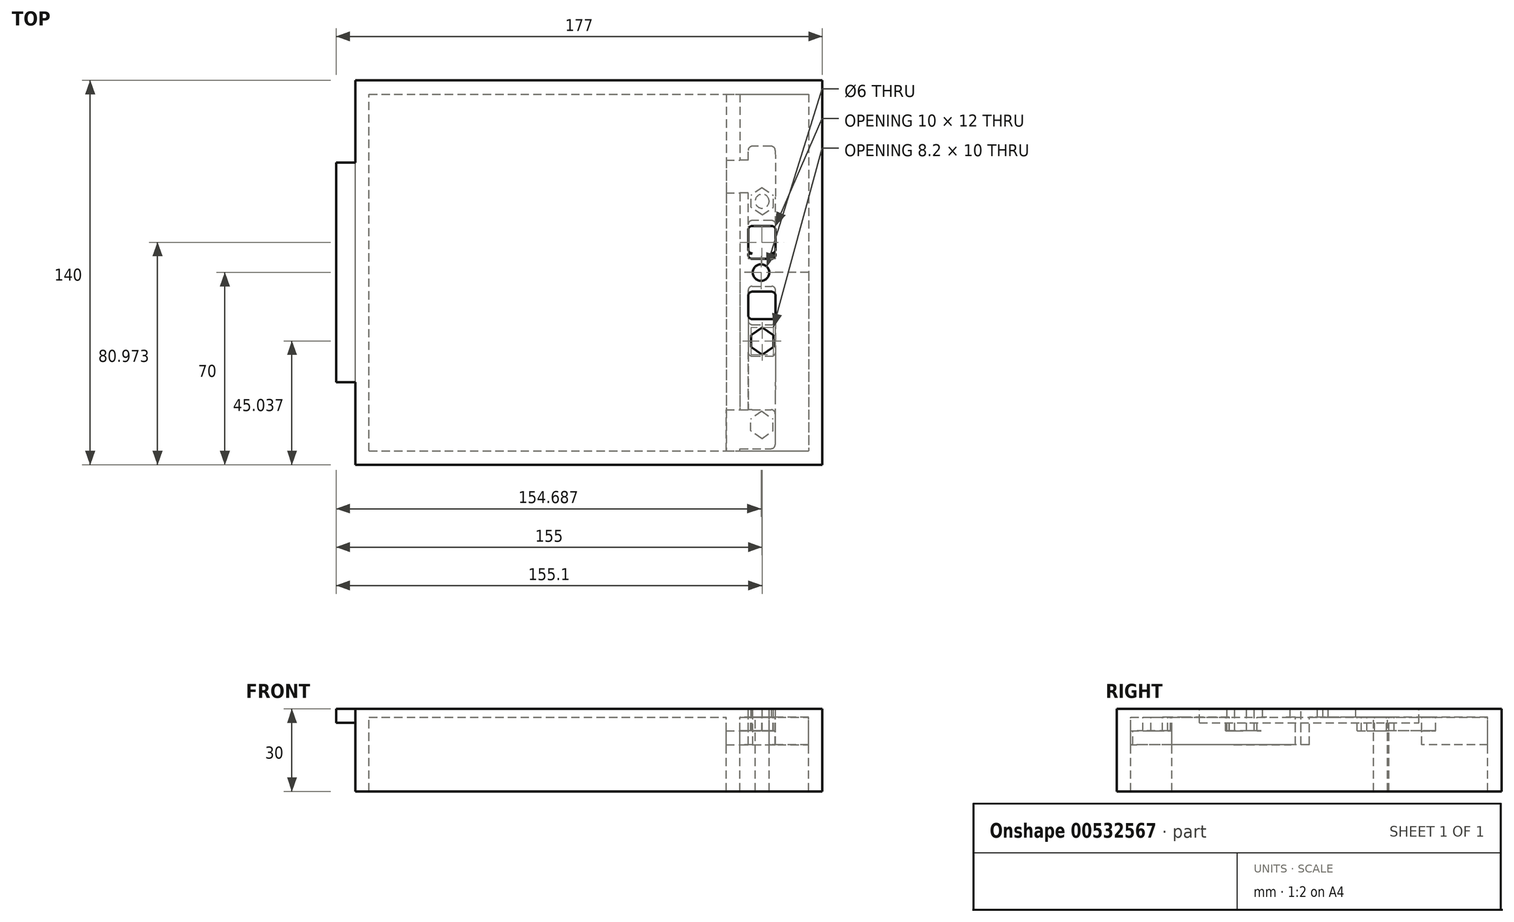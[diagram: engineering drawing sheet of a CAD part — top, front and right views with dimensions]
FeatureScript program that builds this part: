
annotation { "Feature Type Name" : "Feature", "Feature Type Description" : "" }
export const myFeature = defineFeature(function(context is Context, id is Id, definition is map)
    precondition{}
    {
        {
            var Q0;
            Q0=qCreatedBy(makeId("Top.planeOp"),FACE);
            var sketch = newSketch(context, id + "F0", { "sketchPlane" : qUnion([Q0])});
            skLineSegment(sketch, "E0.bottom", {"start": v(-87.5, 70) * mm, "end": v(82.5, 70) * mm});
            skLineSegment(sketch, "E0.top", {"start": v(-82.5, 0) * mm, "end": v(82.5, 0) * mm, "construction": true});
            skLineSegment(sketch, "E0.right", {"start": v(82.5, 70) * mm, "end": v(82.5, 0) * mm});
            skLineSegment(sketch, "E1.bottom", {"start": v(-82.5, 65) * mm, "end": v(77.5, 65) * mm});
            skLineSegment(sketch, "E1.left", {"start": v(-87.5, 65) * mm, "end": v(-87.5, -5) * mm});
            skLineSegment(sketch, "E1.right", {"start": v(77.5, 65) * mm, "end": v(77.5, 0) * mm});
            skLineSegment(sketch, "E2.left", {"start": v(47.5, 65) * mm, "end": v(47.5, 0.9) * mm});
            skLineSegment(sketch, "E2.right", {"start": v(52.5, 65) * mm, "end": v(52.5, 0) * mm});
            skLineSegment(sketch, "E3", {"start": v(47.5, 41) * mm, "end": v(52.5, 41) * mm});
            skLineSegment(sketch, "E4.MirrorCS", {"start": v(47.5, -65) * mm, "end": v(52.5, -65) * mm});
            skLineSegment(sketch, "E5.MirrorCS", {"start": v(47.5, -65) * mm, "end": v(47.5, -0.9) * mm});
            skLineSegment(sketch, "E6.MirrorCS", {"start": v(-82.5, -65) * mm, "end": v(77.5, -65) * mm});
            skLineSegment(sketch, "E7.MirrorCS", {"start": v(-87.5, -65) * mm, "end": v(-87.5, 5) * mm});
            skLineSegment(sketch, "E8.MirrorCS", {"start": v(-87.5, -70) * mm, "end": v(82.5, -70) * mm});
            skLineSegment(sketch, "E9.MirrorCS", {"start": v(82.5, -70) * mm, "end": v(82.5, 0) * mm});
            skLineSegment(sketch, "E10.MirrorCS", {"start": v(57, -4.97) * mm, "end": v(64, -4.97) * mm});
            skLineSegment(sketch, "E11.MirrorCS", {"start": v(55.5, -15.47) * mm, "end": v(55.5, -8.47) * mm});
            skLineSegment(sketch, "E12.MirrorCS", {"start": v(77.5, -65) * mm, "end": v(77.5, 0) * mm});
            skLineSegment(sketch, "E13.MirrorCS", {"start": v(65.5, -15.47) * mm, "end": v(65.5, -8.47) * mm});
            skLineSegment(sketch, "E14.MirrorCS", {"start": v(52.5, -65) * mm, "end": v(52.5, 0) * mm});
            skLineSegment(sketch, "E15", {"start": v(-87.5, -65) * mm, "end": v(-87.5, -70) * mm});
            skLineSegment(sketch, "E16", {"start": v(-87.5, 65) * mm, "end": v(-87.5, 70) * mm});
            skLineSegment(sketch, "E17.left", {"start": v(-177.5, 47.5) * mm, "end": v(-177.5, 0) * mm});
            skCircle(sketch, "E18", {"center": v(-162.5, 30) * mm, "radius": 3.25 * mm});
            skLineSegment(sketch, "E19.left", {"start": v(-147.5, 70) * mm, "end": v(-147.5, 0) * mm});
            skCircle(sketch, "E20.MirrorC", {"center": v(-162.5, -30) * mm, "radius": 3.25 * mm});
            skLineSegment(sketch, "E21.MirrorCS", {"start": v(-147.5, -70) * mm, "end": v(-147.5, 0) * mm});
            skLineSegment(sketch, "E22.MirrorCS", {"start": v(-177.5, -47.5) * mm, "end": v(-177.5, 0) * mm});
            skCircle(sketch, "E23", {"center": v(-162.5, 30) * mm, "radius": 12.5 * mm});
            skCircle(sketch, "E24.MirrorC", {"center": v(-162.5, -30) * mm, "radius": 12.5 * mm});
            skPoint(sketch, "E25", {"position": v(-147.5, -40) * mm});
            skLineSegment(sketch, "E26", {"start": v(-147.5, -40) * mm, "end": v(-142.5, -40) * mm});
            skPoint(sketch, "E27", {"position": v(-147.5, 40) * mm});
            skLineSegment(sketch, "E28", {"start": v(-147.5, 40) * mm, "end": v(-142.5, 40) * mm});
            skLineSegment(sketch, "E29", {"start": v(-94.5, -40) * mm, "end": v(-87.5, -40) * mm});
            skLineSegment(sketch, "E30", {"start": v(-94.5, 40) * mm, "end": v(-87.5, 40) * mm});
            skLineSegment(sketch, "E31", {"start": v(-94.5, -40) * mm, "end": v(-94.5, 40) * mm});
            skLineSegment(sketch, "E32", {"start": v(-142.5, -40) * mm, "end": v(-140.5, -40) * mm});
            skLineSegment(sketch, "E33", {"start": v(-140.5, -40) * mm, "end": v(-140.5, -70) * mm});
            skLineSegment(sketch, "E34", {"start": v(-140.5, -40) * mm, "end": v(-140.5, 70) * mm});
            skLineSegment(sketch, "E35", {"start": v(-142.5, 40) * mm, "end": v(-140.5, 40) * mm});
            skLineSegment(sketch, "E36", {"start": v(-87.5, -70) * mm, "end": v(-82.5, -70) * mm});
            skLineSegment(sketch, "E37", {"start": v(-82.5, -70) * mm, "end": v(-82.5, 65) * mm});
            skLineSegment(sketch, "E38", {"start": v(57, -16.97) * mm, "end": v(64, -16.97) * mm});
            skLineSegment(sketch, "E39", {"start": v(57, -6.97) * mm, "end": v(64, -6.97) * mm});
            skLineSegment(sketch, "E40", {"start": v(57, -18.97) * mm, "end": v(64, -18.97) * mm});
            skLineSegment(sketch, "E41", {"start": v(57, -30.47) * mm, "end": v(64, -30.47) * mm});
            skLineSegment(sketch, "E42", {"start": v(55.5, -51.47) * mm, "end": v(55.5, -58.47) * mm});
            skLineSegment(sketch, "E43", {"start": v(55.5, -64.15) * mm, "end": v(63.86, -64.15) * mm});
            skLineSegment(sketch, "E44", {"start": v(65.36, -58.47) * mm, "end": v(65.36, -51.47) * mm});
            skLineSegment(sketch, "E45", {"start": v(57, -49.97) * mm, "end": v(63.86, -49.97) * mm});
            skCircle(sketch, "E46", {"center": v(60.6, -24.96) * mm, "radius": 2.55 * mm});
            skPoint(sketch, "E47.visualSharp", {"position": v(55.5, -4.97) * mm});
            skArc(sketch, "E47.filletArc", {"start": v(57, -4.97) * mm, "mid": v(55.94, -5.41) * mm, "end": v(55.5, -6.47) * mm});
            skPoint(sketch, "E48.visualSharp", {"position": v(65.5, -4.97) * mm});
            skArc(sketch, "E48.filletArc", {"start": v(65.5, -6.47) * mm, "mid": v(65.06, -5.41) * mm, "end": v(64, -4.97) * mm});
            skPoint(sketch, "E49.newPointA", {"position": v(55.5, -45) * mm});
            skArc(sketch, "E49.filletArc", {"start": v(55.5, -28.97) * mm, "mid": v(55.94, -30.03) * mm, "end": v(57, -30.47) * mm});
            skArc(sketch, "E50.filletArc", {"start": v(64, -30.47) * mm, "mid": v(65.06, -30.03) * mm, "end": v(65.5, -28.97) * mm});
            skLineSegment(sketch, "E51", {"start": v(55.5, -45) * mm, "end": v(55.5, -27.47) * mm});
            skLineSegment(sketch, "E52", {"start": v(65.5, -27.47) * mm, "end": v(65.36, -45) * mm});
            skCircle(sketch, "E53", {"center": v(60.48, -55.5) * mm, "radius": 2.55 * mm});
            skArc(sketch, "E54.MirrorCS", {"start": v(65.5, 6.47) * mm, "mid": v(65.06, 5.41) * mm, "end": v(64, 4.97) * mm});
            skArc(sketch, "E55.MirrorCS", {"start": v(57, 4.97) * mm, "mid": v(55.94, 5.41) * mm, "end": v(55.5, 6.47) * mm});
            skCircle(sketch, "E56.MirrorC", {"center": v(60.6, 25.97) * mm, "radius": 2.55 * mm});
            skLineSegment(sketch, "E57.MirrorCS", {"start": v(57, 6.97) * mm, "end": v(64, 6.97) * mm});
            skPoint(sketch, "E58.MirrorP", {"position": v(65.5, 4.97) * mm});
            skLineSegment(sketch, "E59.MirrorCS", {"start": v(65.5, 15.47) * mm, "end": v(65.5, 8.47) * mm});
            skLineSegment(sketch, "E60.MirrorCS", {"start": v(57, 16.97) * mm, "end": v(64, 16.97) * mm});
            skLineSegment(sketch, "E61.MirrorCS", {"start": v(57, 4.97) * mm, "end": v(64, 4.97) * mm});
            skPoint(sketch, "E62.MirrorP", {"position": v(55.5, 4.97) * mm});
            skLineSegment(sketch, "E63.MirrorCS", {"start": v(57, 18.97) * mm, "end": v(64, 18.97) * mm});
            skLineSegment(sketch, "E64.MirrorCS", {"start": v(55.5, 44.5) * mm, "end": v(55.5, 27.47) * mm});
            skLineSegment(sketch, "E65.MirrorCS", {"start": v(65.5, 27.47) * mm, "end": v(65.37, 44.51) * mm});
            skLineSegment(sketch, "E66.MirrorCS", {"start": v(55.5, 17.47) * mm, "end": v(55.5, 8.47) * mm});
            skLineSegment(sketch, "E67.MirrorCS", {"start": v(65.5, 17.47) * mm, "end": v(65.5, 6.47) * mm});
            skLineSegment(sketch, "E68.MirrorCS", {"start": v(55.5, 6.97) * mm, "end": v(65.5, 6.97) * mm});
            skLineSegment(sketch, "E69.MirrorCS", {"start": v(55.5, 16.97) * mm, "end": v(65.5, 16.97) * mm});
            skLineSegment(sketch, "E70.MirrorCS", {"start": v(55.5, 15.47) * mm, "end": v(55.5, 6.47) * mm});
            skLineSegment(sketch, "E71.MirrorCS", {"start": v(55.5, 18.97) * mm, "end": v(65.5, 18.97) * mm});
            skLineSegment(sketch, "E72", {"start": v(57, 46) * mm, "end": v(63.87, 46) * mm});
            skLineSegment(sketch, "E73", {"start": v(47.5, 29) * mm, "end": v(52.5, 29) * mm});
            skPoint(sketch, "E73.endSnap0", {"position": v(52.5, 32.5) * mm});
            skLineSegment(sketch, "E74", {"start": v(47.5, -50) * mm, "end": v(52.5, -50) * mm});
            skPoint(sketch, "E75.MirrorCS.end.orphan", {"position": v(52.5, -41) * mm});
            skPoint(sketch, "E75.MirrorCS.start.orphan", {"position": v(47.5, -41) * mm});
            skLineSegment(sketch, "E76", {"start": v(-147.5, 70) * mm, "end": v(-140.5, 70) * mm});
            skLineSegment(sketch, "E77", {"start": v(-147.5, -70) * mm, "end": v(-140.5, -70) * mm});
            skLineSegment(sketch, "E78", {"start": v(-147.5, 70) * mm, "end": v(-177.5, 47.5) * mm});
            skLineSegment(sketch, "E79", {"start": v(-147.5, -70) * mm, "end": v(-177.5, -47.5) * mm});
            skLineSegment(sketch, "E80", {"start": v(52.5, 41) * mm, "end": v(55.5, 41) * mm});
            skLineSegment(sketch, "E81", {"start": v(52.5, 29) * mm, "end": v(55.5, 29) * mm});
            skLineSegment(sketch, "E82", {"start": v(52.5, -50) * mm, "end": v(55.5, -50) * mm});
            skLineSegment(sketch, "E83", {"start": v(55.5, -64.15) * mm, "end": v(52.5, -64.15) * mm});
            skLineSegment(sketch, "E84", {"start": v(47.5, 0.9) * mm, "end": v(47.5, -0.9) * mm});
            skLineSegment(sketch, "E85", {"start": v(77.5, 0) * mm, "end": v(52.5, 0) * mm});
            skCircle(sketch, "E86", {"center": v(60.19, 0) * mm, "radius": 3 * mm});
            skLineSegment(sketch, "E87", {"start": v(56.5, 23.83) * mm, "end": v(56.5, 28.1) * mm});
            skLineSegment(sketch, "E88", {"start": v(64.7, 23.83) * mm, "end": v(64.7, 28.1) * mm});
            skPoint(sketch, "E89", {"position": v(60.6, 21) * mm});
            skPoint(sketch, "E90", {"position": v(60.6, 31) * mm});
            skLineSegment(sketch, "E91", {"start": v(60.6, 20.97) * mm, "end": v(56.5, 23.83) * mm});
            skLineSegment(sketch, "E92", {"start": v(60.6, 20.97) * mm, "end": v(64.7, 23.83) * mm});
            skLineSegment(sketch, "E93", {"start": v(60.6, 30.97) * mm, "end": v(64.7, 28.1) * mm});
            skLineSegment(sketch, "E94", {"start": v(60.6, 30.97) * mm, "end": v(56.5, 28.1) * mm});
            skLineSegment(sketch, "E95.MirrorCS", {"start": v(65.18, -52.6) * mm, "end": v(65.18, -52.6) * mm});
            skLineSegment(sketch, "E96", {"start": v(56.38, -57.64) * mm, "end": v(56.38, -53.37) * mm});
            skLineSegment(sketch, "E97", {"start": v(64.58, -57.64) * mm, "end": v(64.58, -53.37) * mm});
            skPoint(sketch, "E98", {"position": v(60.48, -60) * mm});
            skPoint(sketch, "E99", {"position": v(60.48, -50) * mm});
            skLineSegment(sketch, "E100", {"start": v(60.48, -60.5) * mm, "end": v(56.38, -57.64) * mm});
            skLineSegment(sketch, "E101", {"start": v(60.48, -60.5) * mm, "end": v(64.58, -57.64) * mm});
            skLineSegment(sketch, "E102", {"start": v(60.48, -50.5) * mm, "end": v(64.58, -53.37) * mm});
            skLineSegment(sketch, "E103", {"start": v(60.48, -50.5) * mm, "end": v(56.38, -53.37) * mm});
            skLineSegment(sketch, "E104", {"start": v(56.5, -27.1) * mm, "end": v(56.5, -22.82) * mm});
            skLineSegment(sketch, "E105", {"start": v(64.7, -27.1) * mm, "end": v(64.7, -22.82) * mm});
            skPoint(sketch, "E106", {"position": v(60.6, -30) * mm});
            skPoint(sketch, "E107", {"position": v(60.6, -19) * mm});
            skLineSegment(sketch, "E108", {"start": v(60.6, -29.96) * mm, "end": v(56.5, -27.1) * mm});
            skLineSegment(sketch, "E109", {"start": v(60.6, -29.96) * mm, "end": v(64.7, -27.1) * mm});
            skLineSegment(sketch, "E110", {"start": v(60.6, -19.96) * mm, "end": v(64.7, -22.82) * mm});
            skLineSegment(sketch, "E111", {"start": v(60.6, -19.96) * mm, "end": v(56.5, -22.82) * mm});
            skArc(sketch, "E112.filletArc", {"start": v(65.37, 44.51) * mm, "mid": v(64.92, 45.56) * mm, "end": v(63.87, 46) * mm});
            skArc(sketch, "E113.filletArc", {"start": v(57, 46) * mm, "mid": v(55.94, 45.56) * mm, "end": v(55.5, 44.5) * mm});
            skPoint(sketch, "E114.newPointA", {"position": v(55.5, 6.47) * mm});
            skPoint(sketch, "E114.newPointB", {"position": v(55.5, 6.97) * mm});
            skArc(sketch, "E114.filletArc", {"start": v(55.5, 8.47) * mm, "mid": v(55.94, 7.41) * mm, "end": v(57, 6.97) * mm});
            skPoint(sketch, "E115.newPointA", {"position": v(65.5, 6.97) * mm});
            skPoint(sketch, "E115.newPointB", {"position": v(65.5, 6.47) * mm});
            skArc(sketch, "E115.filletArc", {"start": v(64, 6.97) * mm, "mid": v(65.06, 7.41) * mm, "end": v(65.5, 8.47) * mm});
            skPoint(sketch, "E116.newPointA", {"position": v(55.5, 27.47) * mm});
            skPoint(sketch, "E116.newPointB", {"position": v(55.5, 16.97) * mm});
            skArc(sketch, "E116.filletArc", {"start": v(57, 16.97) * mm, "mid": v(55.94, 16.53) * mm, "end": v(55.5, 15.47) * mm});
            skPoint(sketch, "E117.newPointA", {"position": v(65.5, 16.97) * mm});
            skPoint(sketch, "E117.newPointB", {"position": v(65.5, 27.47) * mm});
            skArc(sketch, "E117.filletArc", {"start": v(65.5, 15.47) * mm, "mid": v(65.06, 16.53) * mm, "end": v(64, 16.97) * mm});
            skPoint(sketch, "E118.newPointB", {"position": v(55.5, 18.97) * mm});
            skArc(sketch, "E118.filletArc", {"start": v(57, 18.97) * mm, "mid": v(55.94, 18.53) * mm, "end": v(55.5, 17.47) * mm});
            skPoint(sketch, "E119.newPointB", {"position": v(65.5, 18.97) * mm});
            skArc(sketch, "E119.filletArc", {"start": v(65.5, 17.47) * mm, "mid": v(65.06, 18.53) * mm, "end": v(64, 18.97) * mm});
            skPoint(sketch, "E120.newPointA", {"position": v(55.5, -28.47) * mm});
            skPoint(sketch, "E120.newPointB", {"position": v(55.5, -16.97) * mm});
            skArc(sketch, "E120.filletArc", {"start": v(55.5, -15.47) * mm, "mid": v(55.94, -16.53) * mm, "end": v(57, -16.97) * mm});
            skPoint(sketch, "E121.newPointA", {"position": v(65.5, -16.97) * mm});
            skPoint(sketch, "E121.newPointB", {"position": v(65.5, -28.47) * mm});
            skArc(sketch, "E121.filletArc", {"start": v(64, -16.97) * mm, "mid": v(65.06, -16.53) * mm, "end": v(65.5, -15.47) * mm});
            skLineSegment(sketch, "E122", {"start": v(55.5, -15.47) * mm, "end": v(55.5, -17.47) * mm});
            skLineSegment(sketch, "E123", {"start": v(65.5, -15.47) * mm, "end": v(65.5, -17.47) * mm});
            skPoint(sketch, "E124.newPointB", {"position": v(55.5, -18.97) * mm});
            skArc(sketch, "E124.filletArc", {"start": v(55.5, -17.47) * mm, "mid": v(55.94, -18.53) * mm, "end": v(57, -18.97) * mm});
            skPoint(sketch, "E125.newPointA", {"position": v(65.5, -18.97) * mm});
            skArc(sketch, "E125.filletArc", {"start": v(64, -18.97) * mm, "mid": v(65.06, -18.53) * mm, "end": v(65.5, -17.47) * mm});
            skLineSegment(sketch, "E126", {"start": v(55.5, -17.47) * mm, "end": v(55.5, -27.47) * mm});
            skLineSegment(sketch, "E127", {"start": v(65.5, -27.47) * mm, "end": v(65.5, -17.47) * mm});
            skPoint(sketch, "E128.newPointA", {"position": v(55.5, -6.47) * mm});
            skPoint(sketch, "E128.newPointB", {"position": v(55.5, -6.97) * mm});
            skArc(sketch, "E128.filletArc", {"start": v(57, -6.97) * mm, "mid": v(55.94, -7.41) * mm, "end": v(55.5, -8.47) * mm});
            skPoint(sketch, "E129.newPointA", {"position": v(65.5, -6.97) * mm});
            skPoint(sketch, "E129.newPointB", {"position": v(65.5, -6.47) * mm});
            skArc(sketch, "E129.filletArc", {"start": v(65.5, -8.47) * mm, "mid": v(65.06, -7.41) * mm, "end": v(64, -6.97) * mm});
            skLineSegment(sketch, "E130", {"start": v(55.5, -8.47) * mm, "end": v(55.5, -6.47) * mm});
            skLineSegment(sketch, "E131", {"start": v(65.5, -8.47) * mm, "end": v(65.5, -6.47) * mm});
            skLineSegment(sketch, "E132", {"start": v(55.5, 27.47) * mm, "end": v(55.5, 15.47) * mm});
            skLineSegment(sketch, "E133", {"start": v(65.5, 27.47) * mm, "end": v(65.5, 17.47) * mm});
            skArc(sketch, "E134.filletArc", {"start": v(65.36, -51.47) * mm, "mid": v(64.93, -50.41) * mm, "end": v(63.86, -49.97) * mm});
            skLineSegment(sketch, "E135", {"start": v(65.36, -45) * mm, "end": v(65.36, -51.47) * mm});
            skLineSegment(sketch, "E136", {"start": v(55.5, -45) * mm, "end": v(55.5, -51.47) * mm});
            skLineSegment(sketch, "E137", {"start": v(55.5, -58.47) * mm, "end": v(55.5, -64.15) * mm});
            skLineSegment(sketch, "E138", {"start": v(65.36, -58.47) * mm, "end": v(65.36, -62.65) * mm});
            skPoint(sketch, "E139.visualSharp", {"position": v(65.36, -64.15) * mm});
            skArc(sketch, "E139.filletArc", {"start": v(63.86, -64.15) * mm, "mid": v(64.93, -63.71) * mm, "end": v(65.36, -62.65) * mm});
            skLineSegment(sketch, "E140", {"start": v(57, -49.97) * mm, "end": v(55.5, -50) * mm});
            skSolve(sketch);
        }
        {
            var Q0;
            Q0=makeQuery(id+"F0.imprint","IMPRINT",FACE,{"disambiguationData":[TD([[makeQuery(id+"F0.imprint","IMPRINT",EDGE,{"derivedFrom":sQuery(id+"F0.wireOp",EDGE,"E0.bottom")}),-1.0]])]});
            var Q1;
            {var subQ6=sQuery(id+"F0.wireOp",EDGE,"E73");Q1=makeQuery(id+"F0.imprint","IMPRINT",FACE,{"disambiguationData":[TD([[makeQuery(id+"F0.imprint","IMPRINT",EDGE,{"derivedFrom":subQ6}),-1.0]])]});}
            var Q2;
            {var subQ6=sQuery(id+"F0.wireOp",EDGE,"E74");Q2=makeQuery(id+"F0.imprint","IMPRINT",FACE,{"disambiguationData":[TD([[makeQuery(id+"F0.imprint","IMPRINT",EDGE,{"derivedFrom":subQ6}),-1.0]])]});}
            var Q3;
            {var subQ8=sQuery(id+"F0.wireOp",EDGE,"E65.MirrorCS");Q3=makeQuery(id+"F0.imprint","IMPRINT",FACE,{"disambiguationData":[TD([[makeQuery(id+"F0.imprint","IMPRINT",EDGE,{"derivedFrom":subQ8}),1.0]])]});}
            var Q4;
            Q4=makeQuery(id+"F0.imprint","IMPRINT",FACE,{"disambiguationData":[TD([[makeQuery(id+"F0.imprint","IMPRINT",EDGE,{"derivedFrom":sQuery(id+"F0.wireOp",EDGE,"E41")}),-1.0]])]});
            var Q5;
            {var subQ8=sQuery(id+"F0.wireOp",EDGE,"E118.filletArc");Q5=makeQuery(id+"F0.imprint","IMPRINT",FACE,{"disambiguationData":[TD([[makeQuery(id+"F0.imprint","IMPRINT",EDGE,{"derivedFrom":subQ8}),1.0]])]});}
            var Q6;
            {var subQ5=sQuery(id+"F0.wireOp",EDGE,"E43");Q6=makeQuery(id+"F0.imprint","IMPRINT",FACE,{"disambiguationData":[TD([[makeQuery(id+"F0.imprint","IMPRINT",EDGE,{"derivedFrom":subQ5}),1.0]])]});}
            var Q7;
            Q7=makeQuery(id+"F0.imprint","IMPRINT",FACE,{"disambiguationData":[TD([[makeQuery(id+"F0.imprint","IMPRINT",EDGE,{"derivedFrom":sQuery(id+"F0.wireOp",EDGE,"E10.MirrorCS")}),-1.0]])]});
            var Q8;
            {var subQ5=sQuery(id+"F0.wireOp",EDGE,"E55.MirrorCS");Q8=makeQuery(id+"F0.imprint","IMPRINT",FACE,{"disambiguationData":[TD([[makeQuery(id+"F0.imprint","IMPRINT",EDGE,{"derivedFrom":subQ5}),-1.0]])]});}
            var Q9;
            Q9=makeQuery(id+"F0.imprint","IMPRINT",FACE,{"disambiguationData":[TD([[makeQuery(id+"F0.imprint","IMPRINT",EDGE,{"derivedFrom":sQuery(id+"F0.wireOp",EDGE,"E87")}),-1.0]])]});
            var Q10;
            {var subQ4=sQuery(id+"F0.wireOp",EDGE,"E96");Q10=makeQuery(id+"F0.imprint","IMPRINT",FACE,{"disambiguationData":[TD([[makeQuery(id+"F0.imprint","IMPRINT",EDGE,{"derivedFrom":subQ4}),-1.0]])]});}
            var Q11;
            {var subQ0=sQuery(id+"F0.wireOp",EDGE,"6d39de08-ad94-4231-b662-17a660603f594.MirrorC");var subQ1=sQuery(id+"F0.wireOp",EDGE,"E56.MirrorC");var subQ2=makeQuery(id+"F0.imprint","INTERSECT",VERTEX,{"disambiguationData":[OD(0.0)],"derivedFrom":[subQ1,subQ0]});Q11=makeQuery(id+"F0.imprint","IMPRINT",FACE,{"disambiguationData":[TD([[makeQuery(id+"F0.imprint","IMPRINT",EDGE,{"disambiguationData":[TD([[subQ2,-1.0]])],"derivedFrom":subQ1}),-1.0]])]});}
            var Q12;
            {var subQ5=sQuery(id+"F0.wireOp",EDGE,"E45");Q12=makeQuery(id+"F0.imprint","IMPRINT",FACE,{"disambiguationData":[TD([[makeQuery(id+"F0.imprint","IMPRINT",EDGE,{"derivedFrom":subQ5}),-1.0]])]});}
            var Q13;
            Q13=makeQuery(id+"F0.imprint","IMPRINT",FACE,{"disambiguationData":[TD([[makeQuery(id+"F0.imprint","IMPRINT",EDGE,{"derivedFrom":sQuery(id+"F0.wireOp",EDGE,"E46")}),1.0]])]});
            var Q14;
            Q14=makeQuery(id+"F0.imprint","IMPRINT",FACE,{"disambiguationData":[TD([[makeQuery(id+"F0.imprint","IMPRINT",EDGE,{"derivedFrom":sQuery(id+"F0.wireOp",EDGE,"E46")}),-1.0]])]});
            var Q15;
            {var subQ0=sQuery(id+"F0.wireOp",EDGE,"da70cb73-bd24-4d72-8de4-aa27c8984207.MirrorC");var subQ1=sQuery(id+"F0.wireOp",EDGE,"E53");var subQ2=makeQuery(id+"F0.imprint","INTERSECT",VERTEX,{"disambiguationData":[OD(0.0)],"derivedFrom":[subQ1,subQ0]});Q15=makeQuery(id+"F0.imprint","IMPRINT",FACE,{"disambiguationData":[TD([[makeQuery(id+"F0.imprint","IMPRINT",EDGE,{"disambiguationData":[TD([[subQ2,-1.0]])],"derivedFrom":subQ1}),1.0]])]});}
            var Q16;
            {var subQ0=sQuery(id+"F0.wireOp",EDGE,"da70cb73-bd24-4d72-8de4-aa27c8984207.MirrorC");var subQ1=sQuery(id+"F0.wireOp",EDGE,"E53");var subQ2=makeQuery(id+"F0.imprint","INTERSECT",VERTEX,{"disambiguationData":[OD(0.0)],"derivedFrom":[subQ1,subQ0]});Q16=makeQuery(id+"F0.imprint","IMPRINT",FACE,{"disambiguationData":[TD([[makeQuery(id+"F0.imprint","IMPRINT",EDGE,{"disambiguationData":[TD([[subQ2,1.0]])],"derivedFrom":subQ1}),1.0]])]});}
            var Q17;
            Q17=makeQuery(id+"F0.imprint","IMPRINT",FACE,{"disambiguationData":[TD([[makeQuery(id+"F0.imprint","IMPRINT",EDGE,{"derivedFrom":sQuery(id+"F0.wireOp",EDGE,"E38")}),-1.0]])]});
            var Q18;
            Q18=makeQuery(id+"F0.imprint","IMPRINT",FACE,{"disambiguationData":[TD([[makeQuery(id+"F0.imprint","IMPRINT",EDGE,{"derivedFrom":sQuery(id+"F0.wireOp",EDGE,"E41")}),1.0]])]});
            var Q19;
            {var subQ0=sQuery(id+"F0.wireOp",EDGE,"6d39de08-ad94-4231-b662-17a660603f594.MirrorC");var subQ1=sQuery(id+"F0.wireOp",EDGE,"E56.MirrorC");var subQ2=makeQuery(id+"F0.imprint","INTERSECT",VERTEX,{"disambiguationData":[OD(1.0)],"derivedFrom":[subQ1,subQ0]});Q19=makeQuery(id+"F0.imprint","IMPRINT",FACE,{"disambiguationData":[TD([[makeQuery(id+"F0.imprint","IMPRINT",EDGE,{"disambiguationData":[TD([[subQ2,1.0]])],"derivedFrom":subQ1}),-1.0]])]});}
            var Q20;
            {var subQ0=sQuery(id+"F0.wireOp",EDGE,"6d39de08-ad94-4231-b662-17a660603f594.MirrorC");var subQ1=sQuery(id+"F0.wireOp",EDGE,"E56.MirrorC");var subQ2=makeQuery(id+"F0.imprint","INTERSECT",VERTEX,{"disambiguationData":[OD(0.0)],"derivedFrom":[subQ1,subQ0]});Q20=makeQuery(id+"F0.imprint","IMPRINT",FACE,{"disambiguationData":[TD([[makeQuery(id+"F0.imprint","IMPRINT",EDGE,{"disambiguationData":[TD([[subQ2,-1.0]])],"derivedFrom":subQ1}),1.0]])]});}
            var Q21;
            {var subQ0=sQuery(id+"F0.wireOp",EDGE,"da70cb73-bd24-4d72-8de4-aa27c8984207.MirrorC");var subQ1=sQuery(id+"F0.wireOp",EDGE,"E53");var subQ2=makeQuery(id+"F0.imprint","INTERSECT",VERTEX,{"disambiguationData":[OD(0.0)],"derivedFrom":[subQ1,subQ0]});Q21=makeQuery(id+"F0.imprint","IMPRINT",FACE,{"disambiguationData":[TD([[makeQuery(id+"F0.imprint","IMPRINT",EDGE,{"disambiguationData":[TD([[subQ2,-1.0]])],"derivedFrom":subQ1}),-1.0]])]});}
            var Q22;
            {var subQ0=sQuery(id+"F0.wireOp",EDGE,"E101");var subQ1=sQuery(id+"F0.wireOp",EDGE,"JaYlbfzk-Zl2f-mc1O-yia5-9wafT0kwsFXx");var subQ2=makeQuery(id+"F0.imprint","INTERSECT",VERTEX,{"derivedFrom":[subQ1,subQ0]});Q22=makeQuery(id+"F0.imprint","IMPRINT",FACE,{"disambiguationData":[TD([[makeQuery(id+"F0.imprint","IMPRINT",EDGE,{"disambiguationData":[TD([[subQ2,-1.0]])],"derivedFrom":subQ1}),1.0]])]});}
            var Q23;
            {var subQ0=sQuery(id+"F0.wireOp",EDGE,"E111");var subQ1=sQuery(id+"F0.wireOp",EDGE,"E40");var subQ2=makeQuery(id+"F0.imprint","INTERSECT",VERTEX,{"derivedFrom":[subQ1,subQ0]});Q23=makeQuery(id+"F0.imprint","IMPRINT",FACE,{"disambiguationData":[TD([[makeQuery(id+"F0.imprint","IMPRINT",EDGE,{"disambiguationData":[TD([[subQ2,-1.0]])],"derivedFrom":subQ1}),1.0]])]});}
            var Q24;
            {var subQ3=sQuery(id+"F0.wireOp",EDGE,"E119.filletArc");Q24=makeQuery(id+"F0.imprint","IMPRINT",FACE,{"disambiguationData":[TD([[makeQuery(id+"F0.imprint","IMPRINT",EDGE,{"derivedFrom":subQ3}),-1.0]])]});}
            var Q25;
            {var subQ3=sQuery(id+"F0.wireOp",EDGE,"E118.filletArc");Q25=makeQuery(id+"F0.imprint","IMPRINT",FACE,{"disambiguationData":[TD([[makeQuery(id+"F0.imprint","IMPRINT",EDGE,{"derivedFrom":subQ3}),-1.0]])]});}
            var Q26;
            {var subQ3=sQuery(id+"F0.wireOp",EDGE,"E116.filletArc");Q26=makeQuery(id+"F0.imprint","IMPRINT",FACE,{"disambiguationData":[TD([[makeQuery(id+"F0.imprint","IMPRINT",EDGE,{"derivedFrom":subQ3}),-1.0]])]});}
            var Q27;
            {var subQ3=sQuery(id+"F0.wireOp",EDGE,"E117.filletArc");Q27=makeQuery(id+"F0.imprint","IMPRINT",FACE,{"disambiguationData":[TD([[makeQuery(id+"F0.imprint","IMPRINT",EDGE,{"derivedFrom":subQ3}),-1.0]])]});}
            var Q28;
            {var subQ3=sQuery(id+"F0.wireOp",EDGE,"E115.filletArc");Q28=makeQuery(id+"F0.imprint","IMPRINT",FACE,{"disambiguationData":[TD([[makeQuery(id+"F0.imprint","IMPRINT",EDGE,{"derivedFrom":subQ3}),-1.0]])]});}
            var Q29;
            {var subQ3=sQuery(id+"F0.wireOp",EDGE,"E114.filletArc");Q29=makeQuery(id+"F0.imprint","IMPRINT",FACE,{"disambiguationData":[TD([[makeQuery(id+"F0.imprint","IMPRINT",EDGE,{"derivedFrom":subQ3}),-1.0]])]});}
            var Q30;
            Q30=makeQuery(id+"F0.imprint","IMPRINT",FACE,{"disambiguationData":[TD([[makeQuery(id+"F0.imprint","IMPRINT",EDGE,{"derivedFrom":sQuery(id+"F0.wireOp",EDGE,"E10.MirrorCS")}),1.0]])]});
            var Q31;
            {var subQ1=sQuery(id+"F0.wireOp",EDGE,"E1.right");Q31=makeQuery(id+"F0.imprint","IMPRINT",FACE,{"disambiguationData":[TD([[makeQuery(id+"F0.imprint","IMPRINT",EDGE,{"derivedFrom":subQ1}),-1.0]])]});}
            var Q32;
            {var subQ0=sQuery(id+"F0.wireOp",EDGE,"E82");Q32=makeQuery(id+"F0.imprint","IMPRINT",FACE,{"disambiguationData":[TD([[makeQuery(id+"F0.imprint","IMPRINT",EDGE,{"derivedFrom":subQ0}),-1.0]])]});}
            var Q33;
            {var subQ0=sQuery(id+"F0.wireOp",EDGE,"E3");Q33=makeQuery(id+"F0.imprint","IMPRINT",FACE,{"disambiguationData":[TD([[makeQuery(id+"F0.imprint","IMPRINT",EDGE,{"derivedFrom":subQ0}),-1.0]])]});}
            var Q34;
            {var subQ0=sQuery(id+"F0.wireOp",EDGE,"E80");Q34=makeQuery(id+"F0.imprint","IMPRINT",FACE,{"disambiguationData":[TD([[makeQuery(id+"F0.imprint","IMPRINT",EDGE,{"derivedFrom":subQ0}),-1.0]])]});}
            var Q35;
            {var subQ5=sQuery(id+"F0.wireOp",EDGE,"E3");Q35=makeQuery(id+"F0.imprint","IMPRINT",FACE,{"disambiguationData":[TD([[makeQuery(id+"F0.imprint","IMPRINT",EDGE,{"derivedFrom":subQ5}),1.0]])]});}
            var Q36;
            Q36=makeQuery(id+"F0.imprint","IMPRINT",FACE,{"disambiguationData":[TD([[makeQuery(id+"F0.imprint","IMPRINT",EDGE,{"derivedFrom":sQuery(id+"F0.wireOp",EDGE,"E53")}),1.0]])]});
            var Q37;
            Q37=makeQuery(id+"F0.imprint","IMPRINT",FACE,{"disambiguationData":[TD([[makeQuery(id+"F0.imprint","IMPRINT",EDGE,{"derivedFrom":sQuery(id+"F0.wireOp",EDGE,"E56.MirrorC")}),-1.0]])]});
            extrude(context, id + "F1", {"entities" : qUnion([Q0, Q1, Q2, Q3, Q4, Q5, Q6, Q7, Q8, Q9, Q10, Q11, Q12, Q13, Q14, Q15, Q16, Q17, Q18, Q19, Q20, Q21, Q22, Q23, Q24, Q25, Q26, Q27, Q28, Q29, Q30, Q31, Q32, Q33, Q34, Q35, Q36, Q37]), "oppositeDirection" : true, "depth" : 30 * mm, "offsetDistance" : 25 * mm});
        }
        {
            var Q0;
            {var subQ1=sQuery(id+"F0.wireOp",EDGE,"E1.right");Q0=makeQuery(id+"F0.imprint","IMPRINT",FACE,{"disambiguationData":[TD([[makeQuery(id+"F0.imprint","IMPRINT",EDGE,{"derivedFrom":subQ1}),-1.0]])]});}
            var Q1;
            Q1=makeQuery(id+"F0.imprint","IMPRINT",FACE,{"disambiguationData":[TD([[makeQuery(id+"F0.imprint","IMPRINT",EDGE,{"derivedFrom":sQuery(id+"F0.wireOp",EDGE,"E10.MirrorCS")}),1.0]])]});
            var Q2;
            {var subQ5=sQuery(id+"F0.wireOp",EDGE,"E3");Q2=makeQuery(id+"F0.imprint","IMPRINT",FACE,{"disambiguationData":[TD([[makeQuery(id+"F0.imprint","IMPRINT",EDGE,{"derivedFrom":subQ5}),1.0]])]});}
            extrude(context, id + "F2", {"entities" : qUnion([Q0, Q1, Q2]), "operationType" : NewBodyOperationType.REMOVE, "oppositeDirection" : true, "depth" : 30 * mm, "offsetDistance" : 25 * mm, "hasSecondDirection" : true, "secondDirectionOppositeDirection" : true, "secondDirectionDepth" : 13 * mm});
        }
        {
            var Q0;
            {var subQ8=sQuery(id+"F0.wireOp",EDGE,"E118.filletArc");Q0=makeQuery(id+"F0.imprint","IMPRINT",FACE,{"disambiguationData":[TD([[makeQuery(id+"F0.imprint","IMPRINT",EDGE,{"derivedFrom":subQ8}),1.0]])]});}
            var Q1;
            {var subQ5=sQuery(id+"F0.wireOp",EDGE,"E55.MirrorCS");Q1=makeQuery(id+"F0.imprint","IMPRINT",FACE,{"disambiguationData":[TD([[makeQuery(id+"F0.imprint","IMPRINT",EDGE,{"derivedFrom":subQ5}),-1.0]])]});}
            var Q2;
            {var subQ3=sQuery(id+"F0.wireOp",EDGE,"E116.filletArc");Q2=makeQuery(id+"F0.imprint","IMPRINT",FACE,{"disambiguationData":[TD([[makeQuery(id+"F0.imprint","IMPRINT",EDGE,{"derivedFrom":subQ3}),-1.0]])]});}
            var Q3;
            {var subQ3=sQuery(id+"F0.wireOp",EDGE,"E117.filletArc");Q3=makeQuery(id+"F0.imprint","IMPRINT",FACE,{"disambiguationData":[TD([[makeQuery(id+"F0.imprint","IMPRINT",EDGE,{"derivedFrom":subQ3}),-1.0]])]});}
            var Q4;
            {var subQ3=sQuery(id+"F0.wireOp",EDGE,"E115.filletArc");Q4=makeQuery(id+"F0.imprint","IMPRINT",FACE,{"disambiguationData":[TD([[makeQuery(id+"F0.imprint","IMPRINT",EDGE,{"derivedFrom":subQ3}),-1.0]])]});}
            var Q5;
            {var subQ3=sQuery(id+"F0.wireOp",EDGE,"E114.filletArc");Q5=makeQuery(id+"F0.imprint","IMPRINT",FACE,{"disambiguationData":[TD([[makeQuery(id+"F0.imprint","IMPRINT",EDGE,{"derivedFrom":subQ3}),-1.0]])]});}
            var Q6;
            Q6=makeQuery(id+"F0.imprint","IMPRINT",FACE,{"disambiguationData":[TD([[makeQuery(id+"F0.imprint","IMPRINT",EDGE,{"derivedFrom":sQuery(id+"F0.wireOp",EDGE,"E10.MirrorCS")}),-1.0]])]});
            var Q7;
            Q7=makeQuery(id+"F0.imprint","IMPRINT",FACE,{"disambiguationData":[TD([[makeQuery(id+"F0.imprint","IMPRINT",EDGE,{"derivedFrom":sQuery(id+"F0.wireOp",EDGE,"E38")}),-1.0]])]});
            var Q8;
            {var subQ4=sQuery(id+"F0.wireOp",EDGE,"E96");Q8=makeQuery(id+"F0.imprint","IMPRINT",FACE,{"disambiguationData":[TD([[makeQuery(id+"F0.imprint","IMPRINT",EDGE,{"derivedFrom":subQ4}),-1.0]])]});}
            var Q9;
            Q9=makeQuery(id+"F0.imprint","IMPRINT",FACE,{"disambiguationData":[TD([[makeQuery(id+"F0.imprint","IMPRINT",EDGE,{"derivedFrom":sQuery(id+"F0.wireOp",EDGE,"E46")}),1.0]])]});
            var Q10;
            Q10=makeQuery(id+"F0.imprint","IMPRINT",FACE,{"disambiguationData":[TD([[makeQuery(id+"F0.imprint","IMPRINT",EDGE,{"derivedFrom":sQuery(id+"F0.wireOp",EDGE,"E46")}),-1.0]])]});
            var Q11;
            Q11=makeQuery(id+"F0.imprint","IMPRINT",FACE,{"disambiguationData":[TD([[makeQuery(id+"F0.imprint","IMPRINT",EDGE,{"derivedFrom":sQuery(id+"F0.wireOp",EDGE,"E53")}),1.0]])]});
            var Q12;
            {var subQ1=sQuery(id+"F0.wireOp",EDGE,"E41");Q12=makeQuery(id+"F0.imprint","IMPRINT",FACE,{"disambiguationData":[TD([[makeQuery(id+"F0.imprint","IMPRINT",EDGE,{"derivedFrom":subQ1}),-1.0]])]});}
            var Q13;
            Q13=makeQuery(id+"F0.imprint","IMPRINT",FACE,{"disambiguationData":[TD([[makeQuery(id+"F0.imprint","IMPRINT",EDGE,{"derivedFrom":sQuery(id+"F0.wireOp",EDGE,"E87")}),-1.0]])]});
            var Q14;
            Q14=makeQuery(id+"F0.imprint","IMPRINT",FACE,{"disambiguationData":[TD([[makeQuery(id+"F0.imprint","IMPRINT",EDGE,{"derivedFrom":sQuery(id+"F0.wireOp",EDGE,"E56.MirrorC")}),-1.0]])]});
            extrude(context, id + "F3", {"entities" : qUnion([Q0, Q1, Q2, Q3, Q4, Q5, Q6, Q7, Q8, Q9, Q10, Q11, Q12, Q13, Q14]), "operationType" : NewBodyOperationType.REMOVE, "oppositeDirection" : true, "depth" : 30 * mm, "offsetDistance" : 25 * mm, "hasSecondDirection" : true, "secondDirectionOppositeDirection" : true, "secondDirectionDepth" : 3 * mm});
        }
        {
            var Q0;
            {var subQ7=sQuery(id+"F0.wireOp",EDGE,"E65.MirrorCS");Q0=makeQuery(id+"F0.imprint","IMPRINT",FACE,{"disambiguationData":[TD([[makeQuery(id+"F0.imprint","IMPRINT",EDGE,{"derivedFrom":subQ7}),1.0]])]});}
            var Q1;
            {var subQ3=sQuery(id+"F0.wireOp",EDGE,"E119.filletArc");Q1=makeQuery(id+"F0.imprint","IMPRINT",FACE,{"disambiguationData":[TD([[makeQuery(id+"F0.imprint","IMPRINT",EDGE,{"derivedFrom":subQ3}),-1.0]])]});}
            var Q2;
            {var subQ3=sQuery(id+"F0.wireOp",EDGE,"E118.filletArc");Q2=makeQuery(id+"F0.imprint","IMPRINT",FACE,{"disambiguationData":[TD([[makeQuery(id+"F0.imprint","IMPRINT",EDGE,{"derivedFrom":subQ3}),-1.0]])]});}
            var Q3;
            {var subQ8=sQuery(id+"F0.wireOp",EDGE,"E118.filletArc");Q3=makeQuery(id+"F0.imprint","IMPRINT",FACE,{"disambiguationData":[TD([[makeQuery(id+"F0.imprint","IMPRINT",EDGE,{"derivedFrom":subQ8}),1.0]])]});}
            var Q4;
            {var subQ5=sQuery(id+"F0.wireOp",EDGE,"E55.MirrorCS");Q4=makeQuery(id+"F0.imprint","IMPRINT",FACE,{"disambiguationData":[TD([[makeQuery(id+"F0.imprint","IMPRINT",EDGE,{"derivedFrom":subQ5}),-1.0]])]});}
            var Q5;
            Q5=makeQuery(id+"F0.imprint","IMPRINT",FACE,{"disambiguationData":[TD([[makeQuery(id+"F0.imprint","IMPRINT",EDGE,{"derivedFrom":sQuery(id+"F0.wireOp",EDGE,"E10.MirrorCS")}),-1.0]])]});
            var Q6;
            Q6=makeQuery(id+"F0.imprint","IMPRINT",FACE,{"disambiguationData":[TD([[makeQuery(id+"F0.imprint","IMPRINT",EDGE,{"derivedFrom":sQuery(id+"F0.wireOp",EDGE,"E38")}),-1.0]])]});
            var Q7;
            Q7=makeQuery(id+"F0.imprint","IMPRINT",FACE,{"disambiguationData":[TD([[makeQuery(id+"F0.imprint","IMPRINT",EDGE,{"derivedFrom":sQuery(id+"F0.wireOp",EDGE,"E40")}),-1.0]])]});
            var Q8;
            {var subQ2=sQuery(id+"F0.wireOp",EDGE,"E42");Q8=makeQuery(id+"F0.imprint","IMPRINT",FACE,{"disambiguationData":[TD([[makeQuery(id+"F0.imprint","IMPRINT",EDGE,{"derivedFrom":subQ2}),-1.0]])]});}
            var Q9;
            {var subQ6=sQuery(id+"F0.wireOp",EDGE,"E74");Q9=makeQuery(id+"F0.imprint","IMPRINT",FACE,{"disambiguationData":[TD([[makeQuery(id+"F0.imprint","IMPRINT",EDGE,{"derivedFrom":subQ6}),-1.0]])]});}
            var Q10;
            {var subQ0=sQuery(id+"F0.wireOp",EDGE,"E80");Q10=makeQuery(id+"F0.imprint","IMPRINT",FACE,{"disambiguationData":[TD([[makeQuery(id+"F0.imprint","IMPRINT",EDGE,{"derivedFrom":subQ0}),-1.0]])]});}
            var Q11;
            {var subQ0=sQuery(id+"F0.wireOp",EDGE,"E3");Q11=makeQuery(id+"F0.imprint","IMPRINT",FACE,{"disambiguationData":[TD([[makeQuery(id+"F0.imprint","IMPRINT",EDGE,{"derivedFrom":subQ0}),-1.0]])]});}
            var Q12;
            {var subQ1=sQuery(id+"F0.wireOp",EDGE,"E42");Q12=makeQuery(id+"F0.imprint","IMPRINT",FACE,{"disambiguationData":[TD([[makeQuery(id+"F0.imprint","IMPRINT",EDGE,{"derivedFrom":subQ1}),1.0]])]});}
            extrude(context, id + "F4", {"entities" : qUnion([Q0, Q1, Q2, Q3, Q4, Q5, Q6, Q7, Q8, Q9, Q10, Q11, Q12]), "operationType" : NewBodyOperationType.REMOVE, "oppositeDirection" : true, "depth" : 30 * mm, "offsetDistance" : 25 * mm, "hasSecondDirection" : true, "secondDirectionOppositeDirection" : true, "secondDirectionDepth" : 8 * mm});
        }
        {
            var Q0;
            {var subQ0=sQuery(id+"F0.wireOp",EDGE,"E84");Q0=makeQuery(id+"F0.imprint","IMPRINT",FACE,{"disambiguationData":[TD([[makeQuery(id+"F0.imprint","IMPRINT",EDGE,{"derivedFrom":subQ0}),-1.0]])]});}
            extrude(context, id + "F5", {"entities" : qUnion([Q0]), "operationType" : NewBodyOperationType.ADD, "oppositeDirection" : true, "depth" : 3 * mm, "offsetDistance" : 25 * mm});
        }
        {
            var Q0;
            {var subQ4=sQuery(id+"F0.wireOp",EDGE,"E29");Q0=makeQuery(id+"F0.imprint","IMPRINT",FACE,{"disambiguationData":[TD([[makeQuery(id+"F0.imprint","IMPRINT",EDGE,{"derivedFrom":subQ4}),1.0]])]});}
            extrude(context, id + "F6", {"entities" : qUnion([Q0]), "operationType" : NewBodyOperationType.ADD, "oppositeDirection" : true, "depth" : 5 * mm, "offsetDistance" : 25 * mm});
        }
    });
